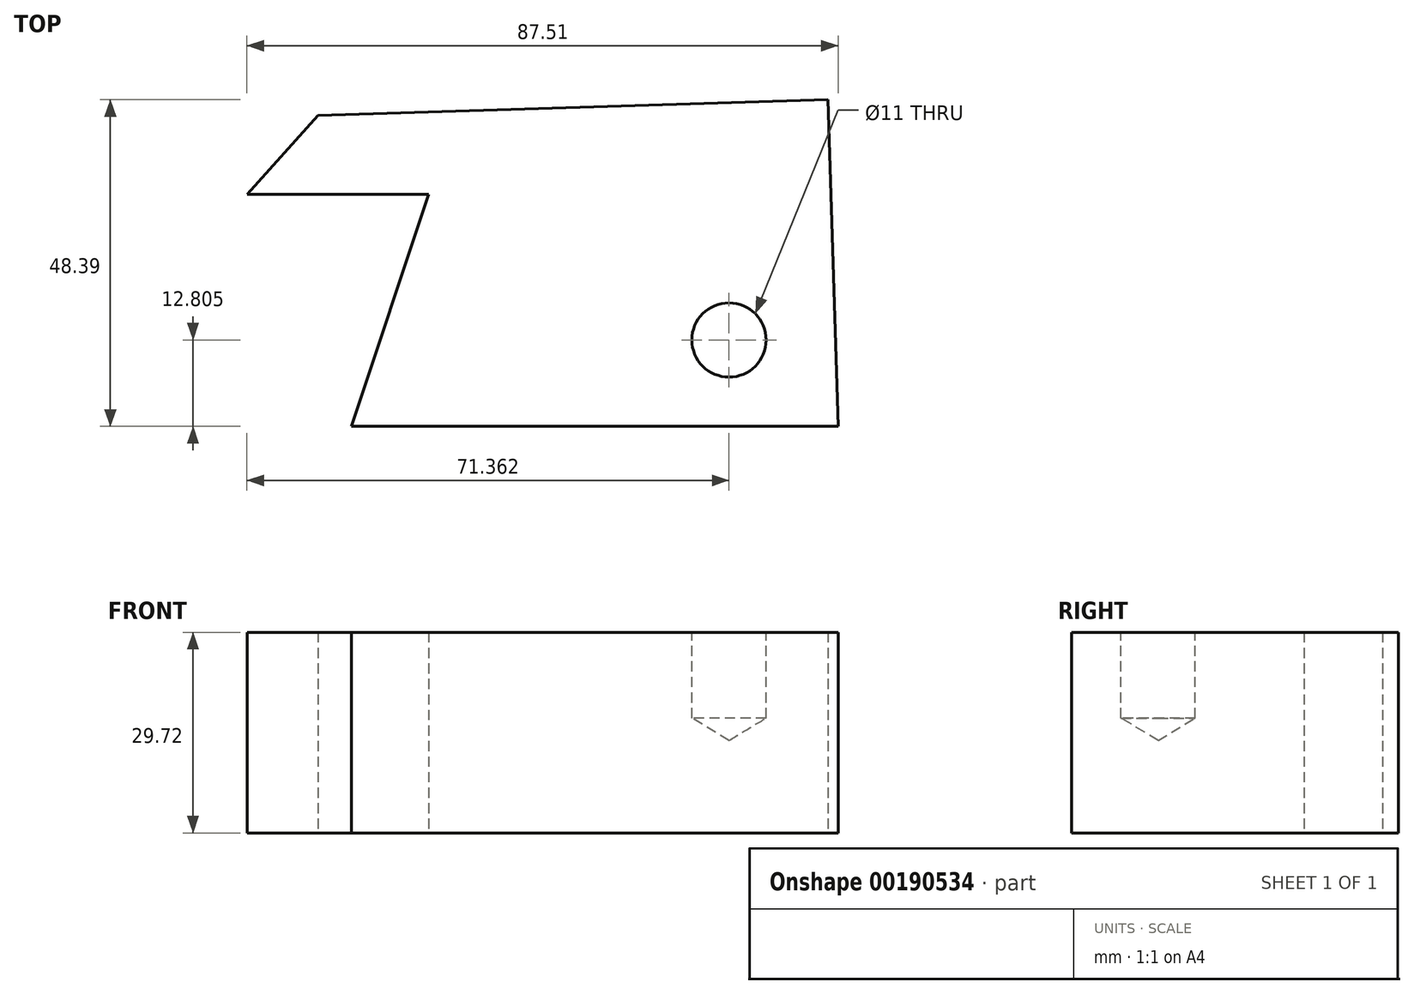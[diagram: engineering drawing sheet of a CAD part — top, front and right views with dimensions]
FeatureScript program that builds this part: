
annotation { "Feature Type Name" : "Feature", "Feature Type Description" : "" }
export const myFeature = defineFeature(function(context is Context, id is Id, definition is map)
    precondition{}
    {
        {
            var Q0;
            Q0=qCreatedBy(makeId("Top.planeOp"),FACE);
            var sketch = newSketch(context, id + "F0", { "sketchPlane" : qUnion([Q0])});
            skLineSegment(sketch, "E0", {"start": v(-40.93, 22) * mm, "end": v(34.56, 24.36) * mm});
            skLineSegment(sketch, "E1", {"start": v(34.56, 24.36) * mm, "end": v(36.08, -24.03) * mm});
            skLineSegment(sketch, "E2", {"start": v(36.08, -24.03) * mm, "end": v(-35.94, -24.03) * mm});
            skLineSegment(sketch, "E3", {"start": v(-35.94, -24.03) * mm, "end": v(-24.53, 10.35) * mm});
            skLineSegment(sketch, "E4", {"start": v(-24.53, 10.35) * mm, "end": v(-51.43, 10.35) * mm});
            skLineSegment(sketch, "E5", {"start": v(-51.43, 10.35) * mm, "end": v(-40.93, 22) * mm});
            skSolve(sketch);
        }
        {
            var Q0;
            Q0=makeQuery(id+"F0.imprint","IMPRINT",FACE,{"disambiguationData":[TD([[makeQuery(id+"F0.imprint","IMPRINT",EDGE,{"derivedFrom":sQuery(id+"F0.wireOp",EDGE,"E0")}),-1.0]])]});
            extrude(context, id + "F1", {"entities" : qUnion([Q0]), "depth" : 29.72 * mm});
        }
        {
            var Q0;
            Q0=makeQuery(id+"F1.opExtrude","CAP_FACE",FACE,{"disambiguationData":[OSD([sQuery(id+"F0.wireOp",EDGE,"E0"),sQuery(id+"F0.wireOp",EDGE,"E1"),sQuery(id+"F0.wireOp",EDGE,"E2"),sQuery(id+"F0.wireOp",EDGE,"E3"),sQuery(id+"F0.wireOp",EDGE,"E4"),sQuery(id+"F0.wireOp",EDGE,"E5")])],"isStart":false});
            var sketch = newSketch(context, id + "F2", { "sketchPlane" : qUnion([Q0])});
            skPoint(sketch, "E6", {"position": v(19.93, -11.23) * mm});
            skSolve(sketch);
        }
        {
            var Q0;
            Q0=sQuery(id+"F2.wireOp",VERTEX,"E6");
            var Q1;
            Q1=makeQuery(id+"F1.opExtrude","SWEPT_BODY",BODY,{"disambiguationData":[OSD([sQuery(id+"F0.wireOp",EDGE,"E0"),sQuery(id+"F0.wireOp",EDGE,"E1"),sQuery(id+"F0.wireOp",EDGE,"E2"),sQuery(id+"F0.wireOp",EDGE,"E3"),sQuery(id+"F0.wireOp",EDGE,"E4"),sQuery(id+"F0.wireOp",EDGE,"E5")])]});
            hole(context, id + "F3", {"style" : HoleStyle.SIMPLE, "endStyle" : HoleEndStyle.BLIND, "standardTappedOrClearance" : lookupTablePath({ "standard" : "ISO", "fit" : "Normal", "size" : "M10", "type" : "Clearance" }), "standardBlindInLast" : lookupTablePath({ "fit" : "Standard", "standard" : "ISO", "size" : "M10", "type" : "Clearance" }), "holeDiameter" : 11 * mm, "holeDepth" : 12.7 * mm, "locations" : qUnion([Q0]), "scope" : qUnion([Q1])});
        }
    });
